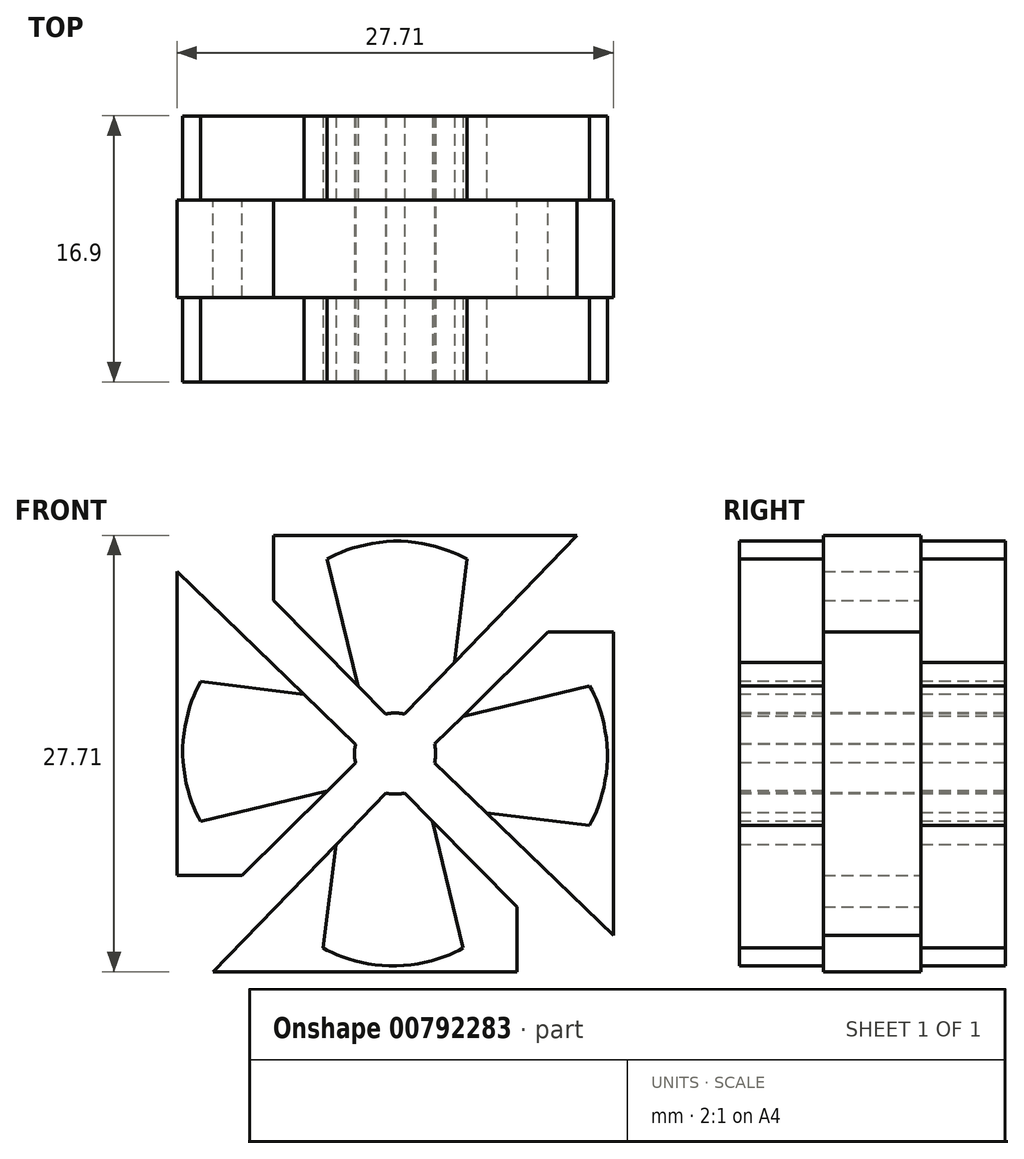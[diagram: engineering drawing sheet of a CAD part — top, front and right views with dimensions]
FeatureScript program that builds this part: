
annotation { "Feature Type Name" : "Feature", "Feature Type Description" : "" }
export const myFeature = defineFeature(function(context is Context, id is Id, definition is map)
    precondition{}
    {
        {
            var Q0;
            Q0=qCreatedBy(makeId("Front.planeOp"),FACE);
            var sketch = newSketch(context, id + "F0", { "sketchPlane" : qUnion([Q0])});
            skLineSegment(sketch, "E0", {"start": v(0, 0) * mm, "end": v(11.57, 11.95) * mm});
            skLineSegment(sketch, "E1", {"start": v(11.57, 11.95) * mm, "end": v(19.3, 4.13) * mm});
            skLineSegment(sketch, "E2", {"start": v(19.3, 4.13) * mm, "end": v(19.3, 0) * mm});
            skLineSegment(sketch, "E3", {"start": v(19.3, 0) * mm, "end": v(0, 0) * mm});
            skSolve(sketch);
        }
        {
            var Q0;
            Q0=makeQuery(id+"F0.imprint","IMPRINT",FACE,{"disambiguationData":[TD([[makeQuery(id+"F0.imprint","IMPRINT",EDGE,{"derivedFrom":sQuery(id+"F0.wireOp",EDGE,"E0")}),-1.0]])]});
            extrude(context, id + "F1", {"entities" : qUnion([Q0]), "endBound" : BoundingType.SYMMETRIC, "depth" : 6.2 * mm, "offsetDistance" : 25 * mm});
        }
        {
            var Q0;
            Q0=qCreatedBy(makeId("Front.planeOp"),FACE);
            var sketch = newSketch(context, id + "F2", { "sketchPlane" : qUnion([Q0])});
            skLineSegment(sketch, "E4.0", {"start": v(0, 0) * mm, "end": v(11.57, 11.95) * mm, "construction": true});
            skLineSegment(sketch, "E5.0", {"start": v(11.57, 11.95) * mm, "end": v(19.3, 4.13) * mm, "construction": true});
            skLineSegment(sketch, "E6", {"start": v(11.57, 11.95) * mm, "end": v(7.8, 8.06) * mm});
            skLineSegment(sketch, "E7", {"start": v(7.8, 8.06) * mm, "end": v(7, 1.51) * mm});
            skLineSegment(sketch, "E8", {"start": v(15.87, 1.51) * mm, "end": v(13.93, 9.56) * mm});
            skLineSegment(sketch, "E9", {"start": v(13.93, 9.56) * mm, "end": v(11.57, 11.95) * mm});
            skFitSpline(sketch, "E10", {"points": [v(7, 1.51) * mm, v(11.4, 0.36) * mm, v(15.87, 1.51) * mm], "startDerivative": vector(5.72, -3.36) * mm, "endDerivative": vector(5.32, 3.4) * mm});
            skSolve(sketch);
        }
        {
            var Q0;
            Q0=makeQuery(id+"F2.imprint","IMPRINT",FACE,{"disambiguationData":[TD([[makeQuery(id+"F2.imprint","IMPRINT",EDGE,{"derivedFrom":sQuery(id+"F2.wireOp",EDGE,"E6")}),1.0]])]});
            extrude(context, id + "F3", {"entities" : qUnion([Q0]), "operationType" : NewBodyOperationType.ADD, "endBound" : BoundingType.SYMMETRIC, "oppositeDirection" : true, "depth" : 16.9 * mm, "offsetDistance" : 25 * mm, "hasSecondDirection" : true, "secondDirectionOppositeDirection" : false, "secondDirectionDepth" : 10.7 * mm});
        }
        {
            var Q0;
            Q0=qCreatedBy(makeId("Top.planeOp"),FACE);
            cPlane(context, id + "F4", {"entities" : qUnion([Q0]), "cplaneType" : CPlaneType.OFFSET, "offset" : 11.95 * mm, "width" : 150 * mm, "height" : 150 * mm});
        }
        {
            var Q0;
            Q0=qCreatedBy(id+"F4.planeOp",FACE);
            cPlane(context, id + "F5", {"entities" : qUnion([Q0]), "cplaneType" : CPlaneType.OFFSET, "offset" : 1.9 * mm, "width" : 150 * mm, "height" : 150 * mm});
        }
        {
            var Q0;
            Q0=qCreatedBy(id+"F5.planeOp",FACE);
            var sketch = newSketch(context, id + "F6", { "sketchPlane" : qUnion([Q0])});
            skLineSegment(sketch, "E11.0", {"start": v(11.57, 8.45) * mm, "end": v(11.57, -8.45) * mm, "construction": true});
            skSolve(sketch);
        }
        {
            var Q0;
            Q0=makeQuery(id+"F3.opExtrude","SWEPT_BODY",BODY,{"disambiguationData":[OSD([sQuery(id+"F2.wireOp",EDGE,"E6"),sQuery(id+"F2.wireOp",EDGE,"E7"),sQuery(id+"F2.wireOp",EDGE,"E8"),sQuery(id+"F2.wireOp",EDGE,"E9"),sQuery(id+"F2.wireOp",EDGE,"E10")])]});
            var Q1;
            Q1=makeQuery(id+"F1.opExtrude","SWEPT_BODY",BODY,{"disambiguationData":[OSD([sQuery(id+"F0.wireOp",EDGE,"E0"),sQuery(id+"F0.wireOp",EDGE,"E1"),sQuery(id+"F0.wireOp",EDGE,"E2"),sQuery(id+"F0.wireOp",EDGE,"E3")])]});
            var Q2;
            Q2=sQuery(id+"F6.wireOp",EDGE,"E11.0");
            circularPattern(context, id + "F7", {"entities" : qUnion([Q0, Q1]), "axis" : qUnion([Q2]), "angle" : 360 * degree, "instanceCount" : 4, "equalSpace" : true});
        }
        {
            var Q0;
            Q0=qCreatedBy(makeId("Front.planeOp"),FACE);
            var sketch = newSketch(context, id + "F8", { "sketchPlane" : qUnion([Q0])});
            skCircle(sketch, "E12", {"center": v(11.57, 13.86) * mm, "radius": 2.58 * mm});
            skLineSegment(sketch, "E13.0", {"start": v(9.66, 13.86) * mm, "end": v(5.77, 17.62) * mm, "construction": true});
            skLineSegment(sketch, "E14.0", {"start": v(7.27, 11.49) * mm, "end": v(9.66, 13.85) * mm, "construction": true});
            skLineSegment(sketch, "E15.0", {"start": v(9.2, 18.15) * mm, "end": v(11.57, 15.76) * mm, "construction": true});
            skLineSegment(sketch, "E16.0", {"start": v(11.57, 15.76) * mm, "end": v(15.33, 19.65) * mm, "construction": true});
            skLineSegment(sketch, "E17.0", {"start": v(15.86, 16.22) * mm, "end": v(13.47, 13.86) * mm, "construction": true});
            skLineSegment(sketch, "E18.0", {"start": v(13.47, 13.85) * mm, "end": v(17.36, 10.1) * mm, "construction": true});
            skLineSegment(sketch, "E19.0", {"start": v(13.93, 9.56) * mm, "end": v(11.57, 11.95) * mm, "construction": true});
            skLineSegment(sketch, "E20.0", {"start": v(11.57, 11.95) * mm, "end": v(7.8, 8.06) * mm, "construction": true});
            skLineSegment(sketch, "E21", {"start": v(9.66, 13.85) * mm, "end": v(13.47, 13.86) * mm, "construction": true});
            skLineSegment(sketch, "E22", {"start": v(11.57, 15.76) * mm, "end": v(11.57, 11.95) * mm, "construction": true});
            skSolve(sketch);
        }
        {
            var Q0;
            Q0 = qSketchRegion(id + "F8", true);
            extrude(context, id + "F9", {"entities" : qUnion([Q0]), "operationType" : NewBodyOperationType.REMOVE, "endBound" : BoundingType.THROUGH_ALL, "oppositeDirection" : true, "depth" : 25 * mm, "offsetDistance" : 25 * mm, "hasSecondDirection" : true, "secondDirectionBound" : SecondDirectionBoundingType.THROUGH_ALL, "secondDirectionOppositeDirection" : false, "secondDirectionDepth" : 25 * mm});
        }
    });
